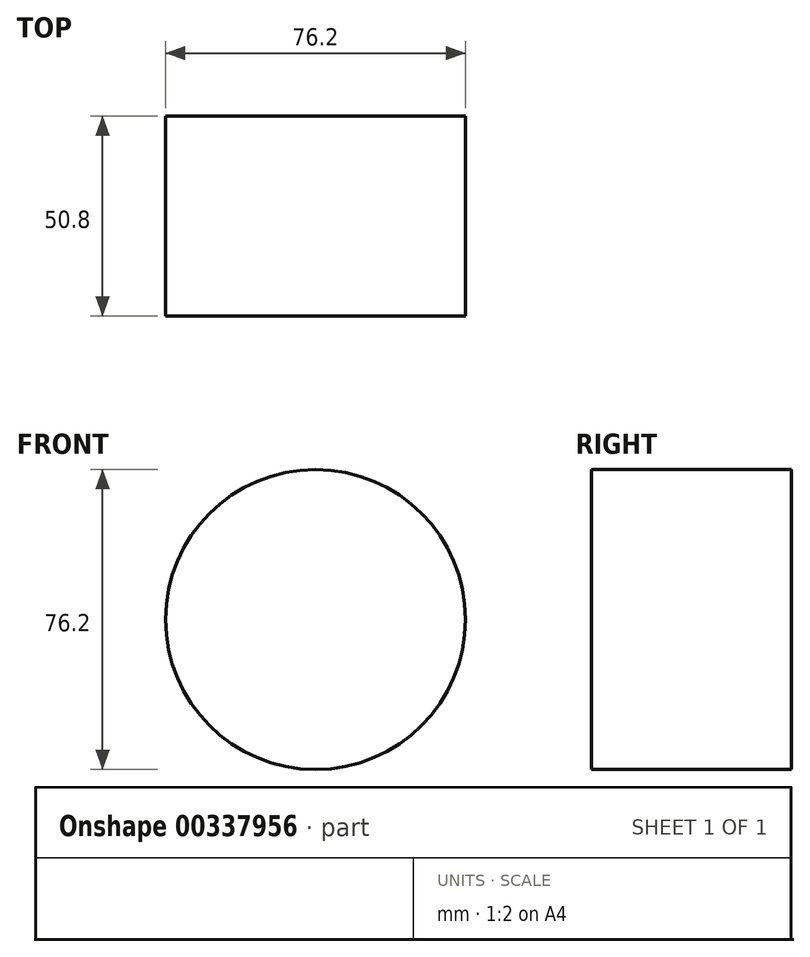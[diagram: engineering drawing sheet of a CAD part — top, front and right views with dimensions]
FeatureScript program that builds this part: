
annotation { "Feature Type Name" : "Feature", "Feature Type Description" : "" }
export const myFeature = defineFeature(function(context is Context, id is Id, definition is map)
    precondition{}
    {
        {
            var Q0;
            Q0=qCreatedBy(makeId("Front.planeOp"),FACE);
            var sketch = newSketch(context, id + "F0", { "sketchPlane" : qUnion([Q0])});
            skCircle(sketch, "E0", {"center": v(0, 0) * mm, "radius": 38.1 * mm});
            skSolve(sketch);
        }
        {
            var Q0;
            Q0 = qSketchRegion(id + "F0", true);
            extrude(context, id + "F1", {"entities" : qUnion([Q0]), "endBound" : BoundingType.SYMMETRIC, "depth" : 50.8 * mm});
        }
    });
